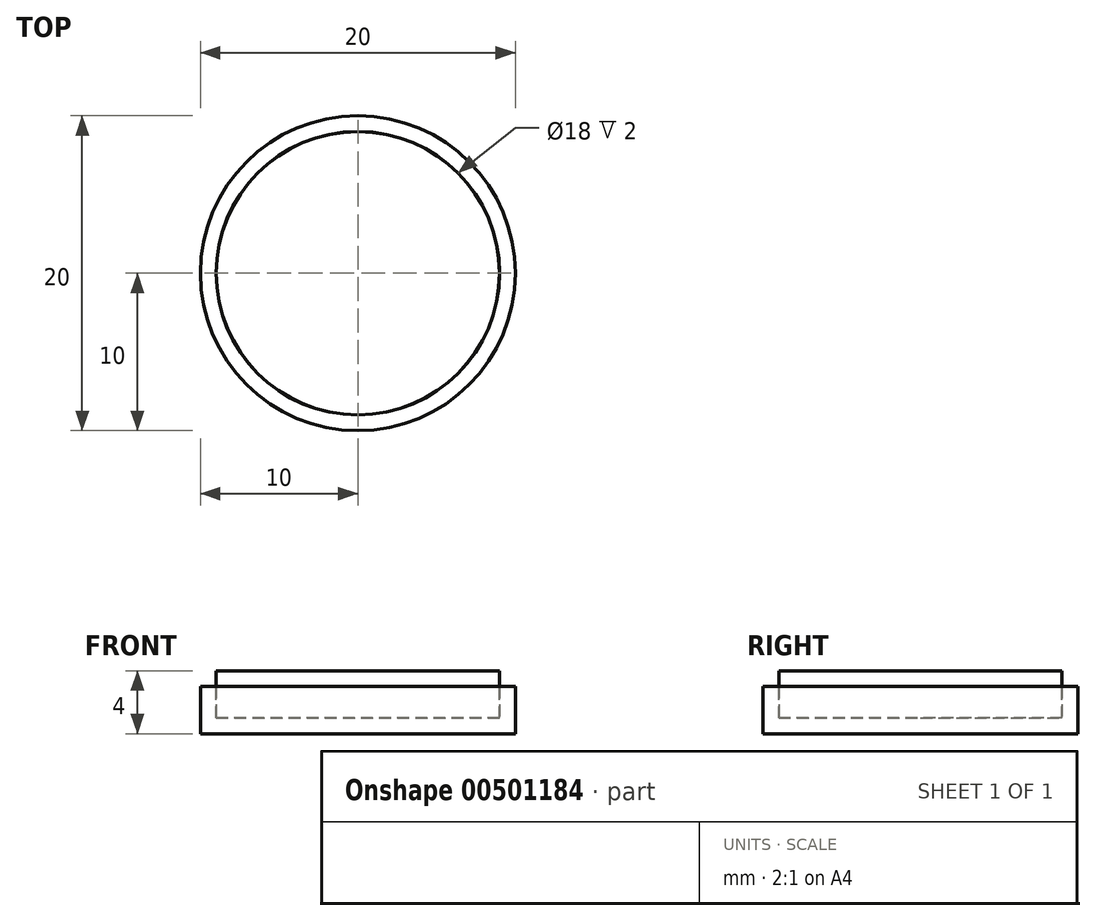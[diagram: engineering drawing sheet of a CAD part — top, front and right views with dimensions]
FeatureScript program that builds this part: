
annotation { "Feature Type Name" : "Feature", "Feature Type Description" : "" }
export const myFeature = defineFeature(function(context is Context, id is Id, definition is map)
    precondition{}
    {
        {
            var Q0;
            Q0=qCreatedBy(makeId("Front.planeOp"),FACE);
            var sketch = newSketch(context, id + "F0", { "sketchPlane" : qUnion([Q0])});
            skLineSegment(sketch, "E0", {"start": v(0, 0) * mm, "end": v(-10, 0) * mm});
            skLineSegment(sketch, "E1", {"start": v(-10, 0) * mm, "end": v(-10, 3) * mm});
            skLineSegment(sketch, "E2", {"start": v(-10, 3) * mm, "end": v(-9, 3) * mm});
            skLineSegment(sketch, "E3", {"start": v(-9, 3) * mm, "end": v(-9, 1) * mm});
            skLineSegment(sketch, "E4", {"start": v(-9, 1) * mm, "end": v(0, 1) * mm});
            skLineSegment(sketch, "E5", {"start": v(0, 1) * mm, "end": v(0, 0) * mm});
            skSolve(sketch);
        }
        {
            var Q0;
            Q0=makeQuery(id+"F0.imprint","IMPRINT",FACE,{"disambiguationData":[TD([[makeQuery(id+"F0.imprint","IMPRINT",EDGE,{"derivedFrom":sQuery(id+"F0.wireOp",EDGE,"E0")}),-1.0]])]});
            var sketch = newSketch(context, id + "F1", { "sketchPlane" : qUnion([Q0])});
            skLineSegment(sketch, "E6", {"start": v(-9, 4) * mm, "end": v(-9, 3) * mm});
            skLineSegment(sketch, "E7", {"start": v(-9, 3) * mm, "end": v(-9, 1) * mm});
            skLineSegment(sketch, "E8", {"start": v(-9, 1) * mm, "end": v(0, 1.01) * mm});
            skLineSegment(sketch, "E9", {"start": v(0, 1.01) * mm, "end": v(0, 4) * mm});
            skLineSegment(sketch, "E10", {"start": v(0, 4) * mm, "end": v(-9, 4) * mm});
            skSolve(sketch);
        }
        {
            var Q0;
            Q0=makeQuery(id+"F1.imprint","IMPRINT",FACE,{"disambiguationData":[TD([[makeQuery(id+"F1.imprint","IMPRINT",EDGE,{"derivedFrom":sQuery(id+"F1.wireOp",EDGE,"E6")}),1.0]])]});
            var Q1;
            Q1=sQuery(id+"F1.wireOp",EDGE,"E9");
            revolve(context, id + "F2", {"entities" : qUnion([Q0]), "axis" : qUnion([Q1]), "revolveType" : RevolveType.FULL});
        }
        {
            var Q0;
            Q0=makeQuery(id+"F0.imprint","IMPRINT",FACE,{"disambiguationData":[TD([[makeQuery(id+"F0.imprint","IMPRINT",EDGE,{"derivedFrom":sQuery(id+"F0.wireOp",EDGE,"E0")}),-1.0]])]});
            var Q1;
            Q1=sQuery(id+"F0.wireOp",EDGE,"E5");
            revolve(context, id + "F3", {"entities" : qUnion([Q0]), "axis" : qUnion([Q1]), "revolveType" : RevolveType.FULL});
        }
    });
